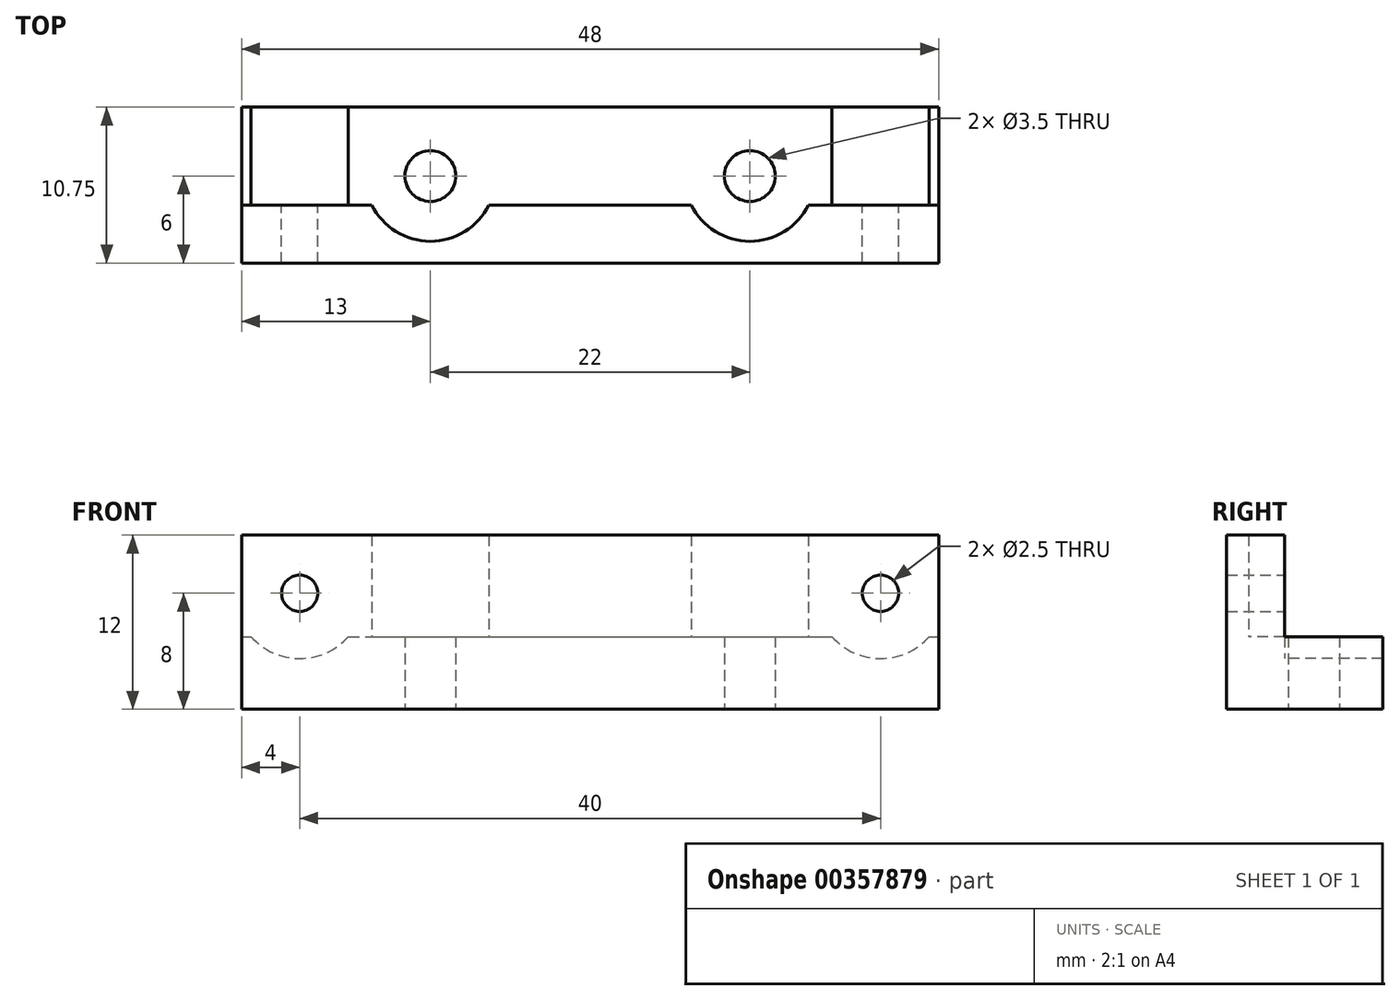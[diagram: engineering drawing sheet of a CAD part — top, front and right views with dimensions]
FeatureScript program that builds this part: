
annotation { "Feature Type Name" : "Feature", "Feature Type Description" : "" }
export const myFeature = defineFeature(function(context is Context, id is Id, definition is map)
    precondition{}
    {
        {
            var Q0;
            Q0=qCreatedBy(makeId("Top.planeOp"),FACE);
            var sketch = newSketch(context, id + "F0", { "sketchPlane" : qUnion([Q0])});
            skLineSegment(sketch, "E0", {"start": v(-32.17, 0) * mm, "end": v(31.92, 0) * mm, "construction": true});
            skLineSegment(sketch, "E1", {"start": v(-11, 2.41) * mm, "end": v(-11, -2.41) * mm, "construction": true});
            skLineSegment(sketch, "E2", {"start": v(11, 2.41) * mm, "end": v(11, -2.41) * mm, "construction": true});
            skLineSegment(sketch, "E3", {"start": v(25, 2.41) * mm, "end": v(25, -2.41) * mm, "construction": true});
            skLineSegment(sketch, "E4", {"start": v(-25, 2.41) * mm, "end": v(-25, -2.41) * mm, "construction": true});
            skLineSegment(sketch, "E5", {"start": v(-31.92, -2) * mm, "end": v(28.52, -2) * mm, "construction": true});
            skSolve(sketch);
        }
        {
            var Q0;
            Q0=qCreatedBy(makeId("Top.planeOp"),FACE);
            var sketch = newSketch(context, id + "F1", { "sketchPlane" : qUnion([Q0])});
            skLineSegment(sketch, "E6.bottom", {"start": v(-24, 4.75) * mm, "end": v(24, 4.75) * mm});
            skLineSegment(sketch, "E6.top", {"start": v(-24, -6) * mm, "end": v(24, -6) * mm});
            skLineSegment(sketch, "E6.left", {"start": v(-24, 4.75) * mm, "end": v(-24, -6) * mm});
            skLineSegment(sketch, "E6.right", {"start": v(24, 4.75) * mm, "end": v(24, -6) * mm});
            skLineSegment(sketch, "E7", {"start": v(-24, -2) * mm, "end": v(24, -2) * mm});
            skCircle(sketch, "E8", {"center": v(11, 0) * mm, "radius": 4.5 * mm});
            skCircle(sketch, "E9", {"center": v(-11, 0) * mm, "radius": 4.5 * mm});
            skSolve(sketch);
        }
        {
            var Q0;
            {var subQ6=sQuery(id+"F1.wireOp",EDGE,"E6.bottom");Q0=makeQuery(id+"F1.imprint","IMPRINT",FACE,{"disambiguationData":[TD([[makeQuery(id+"F1.imprint","IMPRINT",EDGE,{"derivedFrom":subQ6}),-1.0]])]});}
            var Q1;
            {var subQ0=sQuery(id+"F1.wireOp",EDGE,"E9");var subQ1=sQuery(id+"F1.wireOp",EDGE,"E7");var subQ2=makeQuery(id+"F1.imprint","INTERSECT",VERTEX,{"disambiguationData":[OD(0.0)],"derivedFrom":[subQ1,subQ0]});Q1=makeQuery(id+"F1.imprint","IMPRINT",FACE,{"disambiguationData":[TD([[makeQuery(id+"F1.imprint","IMPRINT",EDGE,{"disambiguationData":[TD([[subQ2,-1.0]])],"derivedFrom":subQ1}),1.0]])]});}
            var Q2;
            {var subQ1=sQuery(id+"F1.wireOp",EDGE,"E6.top");Q2=makeQuery(id+"F1.imprint","IMPRINT",FACE,{"disambiguationData":[TD([[makeQuery(id+"F1.imprint","IMPRINT",EDGE,{"derivedFrom":subQ1}),1.0]])]});}
            var Q3;
            {var subQ0=sQuery(id+"F1.wireOp",EDGE,"E9");var subQ1=sQuery(id+"F1.wireOp",EDGE,"E7");var subQ2=makeQuery(id+"F1.imprint","INTERSECT",VERTEX,{"disambiguationData":[OD(0.0)],"derivedFrom":[subQ1,subQ0]});Q3=makeQuery(id+"F1.imprint","IMPRINT",FACE,{"disambiguationData":[TD([[makeQuery(id+"F1.imprint","IMPRINT",EDGE,{"disambiguationData":[TD([[subQ2,-1.0]])],"derivedFrom":subQ1}),-1.0]])]});}
            var Q4;
            {var subQ0=sQuery(id+"F1.wireOp",EDGE,"E8");var subQ1=sQuery(id+"F1.wireOp",EDGE,"E7");var subQ2=makeQuery(id+"F1.imprint","INTERSECT",VERTEX,{"disambiguationData":[OD(0.0)],"derivedFrom":[subQ1,subQ0]});Q4=makeQuery(id+"F1.imprint","IMPRINT",FACE,{"disambiguationData":[TD([[makeQuery(id+"F1.imprint","IMPRINT",EDGE,{"disambiguationData":[TD([[subQ2,-1.0]])],"derivedFrom":subQ1}),-1.0]])]});}
            var Q5;
            {var subQ0=sQuery(id+"F1.wireOp",EDGE,"E8");var subQ1=sQuery(id+"F1.wireOp",EDGE,"E7");var subQ2=makeQuery(id+"F1.imprint","INTERSECT",VERTEX,{"disambiguationData":[OD(0.0)],"derivedFrom":[subQ1,subQ0]});Q5=makeQuery(id+"F1.imprint","IMPRINT",FACE,{"disambiguationData":[TD([[makeQuery(id+"F1.imprint","IMPRINT",EDGE,{"disambiguationData":[TD([[subQ2,-1.0]])],"derivedFrom":subQ1}),1.0]])]});}
            extrude(context, id + "F2", {"entities" : qUnion([Q0, Q1, Q2, Q3, Q4, Q5]), "oppositeDirection" : true, "depth" : 5 * mm});
        }
        {
            var Q0;
            {var subQ0=sQuery(id+"F1.wireOp",EDGE,"E6.top");Q0=makeQuery(id+"F1.imprint","IMPRINT",FACE,{"disambiguationData":[TD([[makeQuery(id+"F1.imprint","IMPRINT",EDGE,{"derivedFrom":subQ0}),1.0]])]});}
            extrude(context, id + "F3", {"entities" : qUnion([Q0]), "operationType" : NewBodyOperationType.ADD, "depth" : 7 * mm});
        }
        {
            var Q0;
            Q0=sQuery(id+"F1.wireOp",VERTEX,"E9.center");
            var Q1;
            Q1=sQuery(id+"F1.wireOp",VERTEX,"E8.center");
            var Q2;
            Q2=makeQuery(id+"F2.opExtrude","SWEPT_BODY",BODY,{"disambiguationData":[OSD([sQuery(id+"F1.wireOp",EDGE,"E6.bottom"),sQuery(id+"F1.wireOp",EDGE,"E6.top"),sQuery(id+"F1.wireOp",EDGE,"E6.left"),sQuery(id+"F1.wireOp",EDGE,"E6.right")])]});
            hole(context, id + "F4", {"style" : HoleStyle.SIMPLE, "endStyle" : HoleEndStyle.BLIND, "holeDiameter" : 3.5 * mm, "holeDepth" : 10 * mm, "isTappedThrough" : true, "tappedDepth" : 12 * mm, "tapClearance" : 3, "locations" : qUnion([Q0, Q1]), "scope" : qUnion([Q2])});
        }
        {
            var Q0;
            Q0=qCreatedBy(makeId("Front.planeOp"),FACE);
            var sketch = newSketch(context, id + "F5", { "sketchPlane" : qUnion([Q0])});
            skLineSegment(sketch, "E10", {"start": v(-20, 13.33) * mm, "end": v(-20, -13.82) * mm, "construction": true});
            skLineSegment(sketch, "E11", {"start": v(20, 16.58) * mm, "end": v(20, -14.96) * mm, "construction": true});
            skLineSegment(sketch, "E12", {"start": v(35.92, 3) * mm, "end": v(-39.07, 3) * mm, "construction": true});
            skCircle(sketch, "E13", {"center": v(-20, 3) * mm, "radius": 1.25 * mm});
            skCircle(sketch, "E14", {"center": v(20, 3) * mm, "radius": 1.25 * mm});
            skCircle(sketch, "E15", {"center": v(-20, 3) * mm, "radius": 4.5 * mm});
            skCircle(sketch, "E16", {"center": v(20, 3) * mm, "radius": 4.5 * mm});
            skSolve(sketch);
        }
        {
            var Q0;
            Q0=makeQuery(id+"F5.imprint","IMPRINT",FACE,{"disambiguationData":[TD([[makeQuery(id+"F5.imprint","IMPRINT",EDGE,{"derivedFrom":sQuery(id+"F5.wireOp",EDGE,"E14")}),-1.0]])]});
            var Q1;
            Q1=makeQuery(id+"F5.imprint","IMPRINT",FACE,{"disambiguationData":[TD([[makeQuery(id+"F5.imprint","IMPRINT",EDGE,{"derivedFrom":sQuery(id+"F5.wireOp",EDGE,"E13")}),-1.0]])]});
            extrude(context, id + "F6", {"entities" : qUnion([Q0, Q1]), "operationType" : NewBodyOperationType.REMOVE, "oppositeDirection" : true, "depth" : 6.4 * mm, "hasSecondDirection" : true, "secondDirectionOppositeDirection" : false, "secondDirectionDepth" : 2 * mm});
        }
        {
            var Q0;
            Q0=makeQuery(id+"F5.imprint","IMPRINT",FACE,{"disambiguationData":[TD([[makeQuery(id+"F5.imprint","IMPRINT",EDGE,{"derivedFrom":sQuery(id+"F5.wireOp",EDGE,"E13")}),1.0]])]});
            var Q1;
            Q1=makeQuery(id+"F5.imprint","IMPRINT",FACE,{"disambiguationData":[TD([[makeQuery(id+"F5.imprint","IMPRINT",EDGE,{"derivedFrom":sQuery(id+"F5.wireOp",EDGE,"E14")}),1.0]])]});
            extrude(context, id + "F7", {"entities" : qUnion([Q0, Q1]), "operationType" : NewBodyOperationType.REMOVE, "depth" : 25 * mm});
        }
    });
